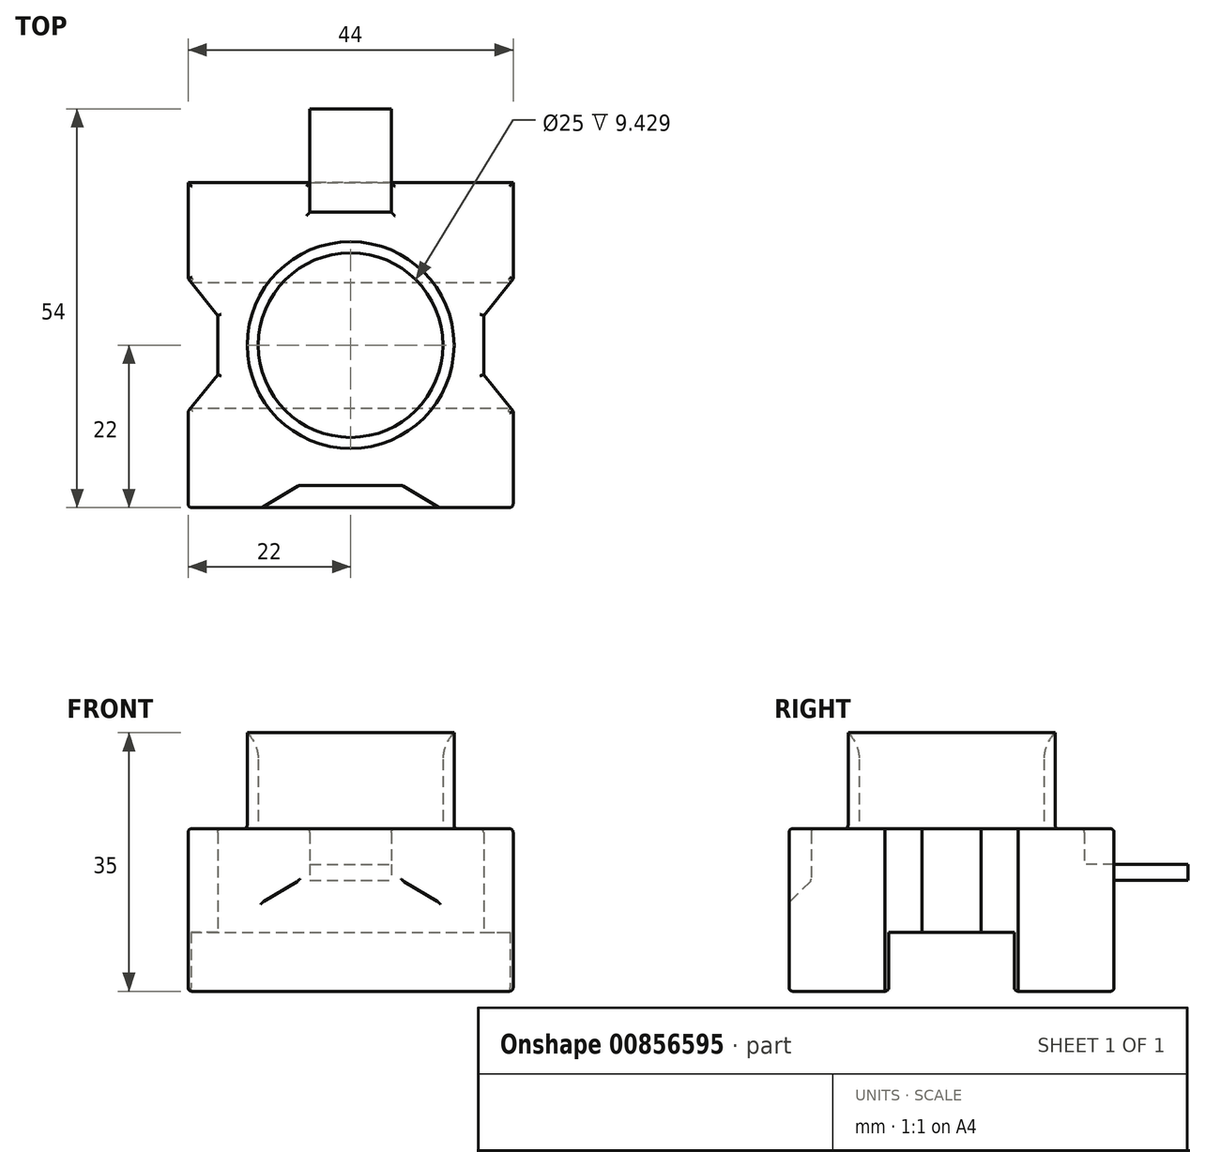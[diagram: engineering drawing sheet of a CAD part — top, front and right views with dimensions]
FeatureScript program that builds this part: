
annotation { "Feature Type Name" : "Feature", "Feature Type Description" : "" }
export const myFeature = defineFeature(function(context is Context, id is Id, definition is map)
    precondition{}
    {
        {
            var Q0;
            Q0=qCreatedBy(makeId("Top.planeOp"),FACE);
            var sketch = newSketch(context, id + "F0", { "sketchPlane" : qUnion([Q0])});
            skLineSegment(sketch, "E0.bottom", {"start": v(22, 22) * mm, "end": v(5.5, 22) * mm});
            skLineSegment(sketch, "E0.top", {"start": v(22, -22) * mm, "end": v(-22, -22) * mm});
            skLineSegment(sketch, "E0.left", {"start": v(22, 22) * mm, "end": v(22, -22) * mm});
            skLineSegment(sketch, "E0.right", {"start": v(-22, 22) * mm, "end": v(-22, 9) * mm});
            skPoint(sketch, "E0.middle", {"position": v(0, 0) * mm});
            skLineSegment(sketch, "E1.trimOffspring", {"start": v(-5.5, 22) * mm, "end": v(-22, 22) * mm});
            skLineSegment(sketch, "E2.MirrorCS", {"start": v(7, -19) * mm, "end": v(-7, -19) * mm});
            skLineSegment(sketch, "E3.MirrorCS", {"start": v(-12, -22) * mm, "end": v(-7, -19) * mm});
            skLineSegment(sketch, "E4.left", {"start": v(-18, 4) * mm, "end": v(-18, -4) * mm});
            skLineSegment(sketch, "E5", {"start": v(-22, 9) * mm, "end": v(-18, 4) * mm});
            skLineSegment(sketch, "E6.MirrorCS", {"start": v(-22, -9) * mm, "end": v(-18, -4) * mm});
            skLineSegment(sketch, "E7.trimOffspring", {"start": v(-22, -9) * mm, "end": v(-22, -22) * mm});
            skLineSegment(sketch, "E8.MirrorCS", {"start": v(22, 9) * mm, "end": v(18, 4) * mm});
            skLineSegment(sketch, "E9.MirrorCS", {"start": v(18, 4) * mm, "end": v(18, -4) * mm});
            skLineSegment(sketch, "E10.MirrorCS", {"start": v(22, -9) * mm, "end": v(18, -4) * mm});
            skLineSegment(sketch, "E11", {"start": v(-22, -9) * mm, "end": v(-22, 9) * mm});
            skLineSegment(sketch, "E12.bottom", {"start": v(5.5, 18) * mm, "end": v(-5.5, 18) * mm});
            skLineSegment(sketch, "E12.left", {"start": v(5.5, 18) * mm, "end": v(5.5, 22) * mm});
            skLineSegment(sketch, "E12.right", {"start": v(-5.5, 18) * mm, "end": v(-5.5, 22) * mm});
            skPoint(sketch, "E12.middle", {"position": v(0, 22) * mm});
            skPoint(sketch, "E13.orphan", {"position": v(-12, 22) * mm});
            skPoint(sketch, "E14.orphan", {"position": v(-5.5, 26) * mm});
            skPoint(sketch, "E15.orphan", {"position": v(5.5, 26) * mm});
            skLineSegment(sketch, "E16", {"start": v(-5.5, 22) * mm, "end": v(5.5, 22) * mm});
            skLineSegment(sketch, "E17.MirrorCS", {"start": v(12, -22) * mm, "end": v(7, -19) * mm});
            skSolve(sketch);
        }
        {
            var Q0;
            Q0=makeQuery(id+"F0.imprint","IMPRINT",FACE,{"disambiguationData":[TD([[makeQuery(id+"F0.imprint","IMPRINT",EDGE,{"derivedFrom":sQuery(id+"F0.wireOp",EDGE,"E0.bottom")}),1.0]])]});
            extrude(context, id + "F1", {"entities" : qUnion([Q0]), "depth" : 22 * mm, "offsetDistance" : 25 * mm});
        }
        {
            var Q0;
            Q0=makeQuery(id+"F0.imprint","IMPRINT",FACE,{"disambiguationData":[TD([[makeQuery(id+"F0.imprint","IMPRINT",EDGE,{"derivedFrom":sQuery(id+"F0.wireOp",EDGE,"E2.MirrorCS")}),1.0]])]});
            extrude(context, id + "F2", {"entities" : qUnion([Q0]), "operationType" : NewBodyOperationType.ADD, "depth" : 17 * mm, "offsetDistance" : 25 * mm});
        }
        {
            var Q0;
            Q0=makeQuery(id+"F2.opExtrude","CAP_EDGE",EDGE,{"disambiguationData":[OSD([sQuery(id+"F0.wireOp",EDGE,"E0.top")])],"isStart":false});
            chamfer(context, id + "F3", {"entities" : qUnion([Q0]), "width" : 5 * mm, "tangentPropagation" : true});
        }
        {
            var Q0;
            {var subQ0=sQuery(id+"F0.wireOp",EDGE,"E0.left");Q0=makeQuery(id+"F1.opExtrude","SWEPT_FACE",FACE,{"disambiguationData":[OSD([subQ0]),TDD([makeQuery(id+"F0.imprint","IMPRINT",EDGE,{"disambiguationData":[TD([[makeQuery(id+"F0.imprint","INTERSECT",VERTEX,{"derivedFrom":[sQuery(id+"F0.wireOp",EDGE,"E0.top"),subQ0]}),1.0]])],"derivedFrom":subQ0})])]});}
            var sketch = newSketch(context, id + "F4", { "sketchPlane" : qUnion([Q0])});
            skLineSegment(sketch, "E18", {"start": v(0, 0) * mm, "end": v(0, 4) * mm});
            skLineSegment(sketch, "E19.bottom", {"start": v(-8.5, 8) * mm, "end": v(8.5, 8) * mm});
            skLineSegment(sketch, "E19.top", {"start": v(-8.5, 0) * mm, "end": v(8.5, 0) * mm});
            skLineSegment(sketch, "E19.left", {"start": v(-8.5, 8) * mm, "end": v(-8.5, 0) * mm});
            skLineSegment(sketch, "E19.right", {"start": v(8.5, 8) * mm, "end": v(8.5, 0) * mm});
            skPoint(sketch, "E19.middle", {"position": v(0, 4) * mm});
            skSolve(sketch);
        }
        {
            var Q0;
            Q0=makeQuery(id+"F4.imprint","IMPRINT",FACE,{"disambiguationData":[TD([[makeQuery(id+"F4.imprint","IMPRINT",EDGE,{"derivedFrom":sQuery(id+"F4.wireOp",EDGE,"E19.bottom")}),-1.0]])]});
            var Q1;
            Q1=makeQuery(id+"F1.opExtrude","SWEPT_FACE",FACE,{"disambiguationData":[OSD([sQuery(id+"F0.wireOp",EDGE,"E0.right")])]});
            extrude(context, id + "F5", {"entities" : qUnion([Q0]), "operationType" : NewBodyOperationType.REMOVE, "endBound" : BoundingType.UP_TO_SURFACE, "oppositeDirection" : true, "depth" : 25 * mm, "endBoundEntityFace" : qUnion([Q1]), "offsetDistance" : 25 * mm});
        }
        {
            var Q0;
            Q0=makeQuery(id+"F0.imprint","IMPRINT",FACE,{"disambiguationData":[TD([[makeQuery(id+"F0.imprint","IMPRINT",EDGE,{"derivedFrom":sQuery(id+"F0.wireOp",EDGE,"E12.bottom")}),-1.0]])]});
            extrude(context, id + "F6", {"entities" : qUnion([Q0]), "operationType" : NewBodyOperationType.ADD, "depth" : 15 * mm, "offsetDistance" : 25 * mm});
        }
        {
            var Q0;
            Q0=makeQuery(id+"F1.opExtrude","SWEPT_FACE",FACE,{"disambiguationData":[OSD([sQuery(id+"F0.wireOp",EDGE,"E12.bottom")])]});
            var sketch = newSketch(context, id + "F7", { "sketchPlane" : qUnion([Q0])});
            skLineSegment(sketch, "E20.bottom", {"start": v(5.5, 15) * mm, "end": v(-5.5, 15) * mm});
            skLineSegment(sketch, "E20.top", {"start": v(5.5, 17.21) * mm, "end": v(-5.5, 17.21) * mm});
            skLineSegment(sketch, "E20.left", {"start": v(5.5, 15) * mm, "end": v(5.5, 17.21) * mm});
            skLineSegment(sketch, "E20.right", {"start": v(-5.5, 15) * mm, "end": v(-5.5, 17.21) * mm});
            skSolve(sketch);
        }
        {
            var Q0;
            Q0=makeQuery(id+"F7.imprint","IMPRINT",FACE,{"disambiguationData":[TD([[makeQuery(id+"F7.imprint","IMPRINT",EDGE,{"derivedFrom":sQuery(id+"F7.wireOp",EDGE,"E20.bottom")}),1.0]])]});
            extrude(context, id + "F8", {"entities" : qUnion([Q0]), "operationType" : NewBodyOperationType.ADD, "depth" : 14 * mm, "offsetDistance" : 25 * mm});
        }
        {
            var Q0;
            Q0=makeQuery(id+"F1.opExtrude","CAP_FACE",FACE,{"disambiguationData":[OSD([sQuery(id+"F0.wireOp",EDGE,"E0.bottom"),sQuery(id+"F0.wireOp",EDGE,"E0.top"),sQuery(id+"F0.wireOp",EDGE,"E0.left"),sQuery(id+"F0.wireOp",EDGE,"E0.right"),sQuery(id+"F0.wireOp",EDGE,"E1.trimOffspring"),sQuery(id+"F0.wireOp",EDGE,"E2.MirrorCS"),sQuery(id+"F0.wireOp",EDGE,"E3.MirrorCS"),sQuery(id+"F0.wireOp",EDGE,"E4.left"),sQuery(id+"F0.wireOp",EDGE,"E5"),sQuery(id+"F0.wireOp",EDGE,"E6.MirrorCS"),sQuery(id+"F0.wireOp",EDGE,"E7.trimOffspring"),sQuery(id+"F0.wireOp",EDGE,"E8.MirrorCS"),sQuery(id+"F0.wireOp",EDGE,"E9.MirrorCS"),sQuery(id+"F0.wireOp",EDGE,"E10.MirrorCS"),sQuery(id+"F0.wireOp",EDGE,"E12.bottom"),sQuery(id+"F0.wireOp",EDGE,"E12.left"),sQuery(id+"F0.wireOp",EDGE,"E12.right"),sQuery(id+"F0.wireOp",EDGE,"E17.MirrorCS")])],"isStart":false});
            var sketch = newSketch(context, id + "F9", { "sketchPlane" : qUnion([Q0])});
            skCircle(sketch, "E21", {"center": v(0, 0) * mm, "radius": 14 * mm});
            skCircle(sketch, "E22", {"center": v(0, 0) * mm, "radius": 12.5 * mm});
            skSolve(sketch);
        }
        {
            var Q0;
            Q0=makeQuery(id+"F9.imprint","IMPRINT",FACE,{"disambiguationData":[TD([[makeQuery(id+"F9.imprint","IMPRINT",EDGE,{"derivedFrom":sQuery(id+"F9.wireOp",EDGE,"E21")}),1.0]])]});
            extrude(context, id + "F10", {"entities" : qUnion([Q0]), "operationType" : NewBodyOperationType.ADD, "depth" : 13 * mm, "offsetDistance" : 25 * mm});
        }
        {
            var Q0;
            Q0=makeQuery(id+"F10.opExtrude","CAP_EDGE",EDGE,{"disambiguationData":[OSD([sQuery(id+"F9.wireOp",EDGE,"E22")])],"isStart":false});
            fillet(context, id + "F11", {"entities" : qUnion([Q0]), "radius" : 5 * mm, "tangentPropagation" : true, "allowEdgeOverflow" : false});
        }
        {
            var Q0;
            {var subQ0=sQuery(id+"F0.wireOp",EDGE,"E17.MirrorCS");var subQ1=sQuery(id+"F0.wireOp",EDGE,"E12.right");var subQ2=sQuery(id+"F0.wireOp",EDGE,"E12.left");var subQ3=sQuery(id+"F0.wireOp",EDGE,"E12.bottom");var subQ4=sQuery(id+"F0.wireOp",EDGE,"E10.MirrorCS");var subQ5=sQuery(id+"F0.wireOp",EDGE,"E9.MirrorCS");var subQ6=sQuery(id+"F0.wireOp",EDGE,"E8.MirrorCS");var subQ7=sQuery(id+"F0.wireOp",EDGE,"E7.trimOffspring");var subQ8=sQuery(id+"F0.wireOp",EDGE,"E6.MirrorCS");var subQ9=sQuery(id+"F0.wireOp",EDGE,"E5");var subQ10=sQuery(id+"F0.wireOp",EDGE,"E0.top");var subQ11=sQuery(id+"F0.wireOp",EDGE,"E3.MirrorCS");var subQ12=sQuery(id+"F0.wireOp",EDGE,"E0.left");var subQ14=sQuery(id+"F0.wireOp",EDGE,"E0.bottom");var subQ15=sQuery(id+"F0.wireOp",EDGE,"E4.left");var subQ16=sQuery(id+"F0.wireOp",EDGE,"E0.right");var subQ17=sQuery(id+"F0.wireOp",EDGE,"E1.trimOffspring");var subQ18=sQuery(id+"F0.wireOp",EDGE,"E2.MirrorCS");Q0=makeQuery(id+"F10.boolean.opBoolean","SPLIT",FACE,{"disambiguationData":[TD([makeQuery(id+"F1.opExtrude","SWEPT_FACE",FACE,{"disambiguationData":[OSD([subQ14])]})])],"derivedFrom":makeQuery(id+"F1.opExtrude","CAP_FACE",FACE,{"disambiguationData":[OSD([subQ14,subQ10,subQ12,subQ16,subQ17,subQ18,subQ11,subQ15,subQ9,subQ8,subQ7,subQ6,subQ5,subQ4,subQ3,subQ2,subQ1,subQ0])],"isStart":false})});}
            var Q1;
            {var subQ0=sQuery(id+"F0.wireOp",EDGE,"E12.right");var subQ1=sQuery(id+"F0.wireOp",EDGE,"E12.left");var subQ2=sQuery(id+"F0.wireOp",EDGE,"E12.bottom");var subQ3=sQuery(id+"F0.wireOp",EDGE,"E1.trimOffspring");var subQ4=sQuery(id+"F0.wireOp",EDGE,"E0.right");var subQ5=sQuery(id+"F0.wireOp",EDGE,"E0.left");var subQ6=sQuery(id+"F0.wireOp",EDGE,"E0.bottom");var subQ7=sQuery(id+"F0.wireOp",EDGE,"E8.MirrorCS");var subQ8=sQuery(id+"F0.wireOp",EDGE,"E5");var subQ9=sQuery(id+"F0.wireOp",EDGE,"E17.MirrorCS");var subQ10=sQuery(id+"F0.wireOp",EDGE,"E3.MirrorCS");var subQ11=sQuery(id+"F0.wireOp",EDGE,"E2.MirrorCS");var subQ12=sQuery(id+"F0.wireOp",EDGE,"E0.top");Q1=makeQuery(id+"F6.boolean.opBoolean","MERGE",FACE,{"derivedFrom":[makeQuery(id+"F5.boolean.opBoolean","SPLIT",FACE,{"disambiguationData":[TD([makeQuery(id+"F1.opExtrude","SWEPT_FACE",FACE,{"disambiguationData":[OSD([subQ6])]})])],"derivedFrom":makeQuery(id+"F2.boolean.opBoolean","MERGE",FACE,{"derivedFrom":[makeQuery(id+"F1.opExtrude","CAP_FACE",FACE,{"disambiguationData":[OSD([subQ6,subQ12,subQ5,subQ4,subQ3,subQ11,subQ10,sQuery(id+"F0.wireOp",EDGE,"E4.left"),subQ8,sQuery(id+"F0.wireOp",EDGE,"E6.MirrorCS"),sQuery(id+"F0.wireOp",EDGE,"E7.trimOffspring"),subQ7,sQuery(id+"F0.wireOp",EDGE,"E9.MirrorCS"),sQuery(id+"F0.wireOp",EDGE,"E10.MirrorCS"),subQ2,subQ1,subQ0,subQ9])],"isStart":true}),makeQuery(id+"F2.opExtrude","CAP_FACE",FACE,{"disambiguationData":[OSD([subQ12,subQ11,subQ10,subQ9])],"isStart":true})]})}),makeQuery(id+"F6.opExtrude","CAP_FACE",FACE,{"disambiguationData":[OSD([subQ2,subQ1,subQ0,sQuery(id+"F0.wireOp",EDGE,"E16")])],"isStart":true})]});}
            var Q2;
            {var subQ0=sQuery(id+"F0.wireOp",EDGE,"E0.left");var subQ1=sQuery(id+"F0.wireOp",EDGE,"E0.top");var subQ3=sQuery(id+"F0.wireOp",EDGE,"E10.MirrorCS");var subQ4=sQuery(id+"F0.wireOp",EDGE,"E7.trimOffspring");var subQ5=sQuery(id+"F0.wireOp",EDGE,"E3.MirrorCS");var subQ6=sQuery(id+"F0.wireOp",EDGE,"E6.MirrorCS");var subQ7=sQuery(id+"F0.wireOp",EDGE,"E17.MirrorCS");var subQ8=sQuery(id+"F0.wireOp",EDGE,"E2.MirrorCS");Q2=makeQuery(id+"F5.boolean.opBoolean","SPLIT",FACE,{"disambiguationData":[TD([makeQuery(id+"F1.opExtrude","SWEPT_FACE",FACE,{"disambiguationData":[OSD([subQ6])]})])],"derivedFrom":makeQuery(id+"F2.boolean.opBoolean","MERGE",FACE,{"derivedFrom":[makeQuery(id+"F1.opExtrude","CAP_FACE",FACE,{"disambiguationData":[OSD([sQuery(id+"F0.wireOp",EDGE,"E0.bottom"),subQ1,subQ0,sQuery(id+"F0.wireOp",EDGE,"E0.right"),sQuery(id+"F0.wireOp",EDGE,"E1.trimOffspring"),subQ8,subQ5,sQuery(id+"F0.wireOp",EDGE,"E4.left"),sQuery(id+"F0.wireOp",EDGE,"E5"),subQ6,subQ4,sQuery(id+"F0.wireOp",EDGE,"E8.MirrorCS"),sQuery(id+"F0.wireOp",EDGE,"E9.MirrorCS"),subQ3,sQuery(id+"F0.wireOp",EDGE,"E12.bottom"),sQuery(id+"F0.wireOp",EDGE,"E12.left"),sQuery(id+"F0.wireOp",EDGE,"E12.right"),subQ7])],"isStart":true}),makeQuery(id+"F2.opExtrude","CAP_FACE",FACE,{"disambiguationData":[OSD([subQ1,subQ8,subQ5,subQ7])],"isStart":true})]})});}
            var Q3;
            Q3=makeQuery(id+"F1.opExtrude","SWEPT_FACE",FACE,{"disambiguationData":[OSD([sQuery(id+"F0.wireOp",EDGE,"E2.MirrorCS")])]});
            var Q4;
            {var subQ0=sQuery(id+"F0.wireOp",EDGE,"E0.top");Q4=makeQuery(id+"F2.boolean.opBoolean","MERGE",FACE,{"derivedFrom":[makeQuery(id+"F1.opExtrude","SWEPT_FACE",FACE,{"disambiguationData":[OSD([subQ0]),TDD([makeQuery(id+"F0.imprint","IMPRINT",EDGE,{"disambiguationData":[TD([[makeQuery(id+"F0.imprint","INTERSECT",VERTEX,{"derivedFrom":[subQ0,sQuery(id+"F0.wireOp",EDGE,"E0.left")]}),-1.0]])],"derivedFrom":subQ0})])]}),makeQuery(id+"F1.opExtrude","SWEPT_FACE",FACE,{"disambiguationData":[OSD([subQ0]),TDD([makeQuery(id+"F0.imprint","IMPRINT",EDGE,{"disambiguationData":[TD([[makeQuery(id+"F0.imprint","INTERSECT",VERTEX,{"derivedFrom":[subQ0,sQuery(id+"F0.wireOp",EDGE,"E7.trimOffspring")]}),1.0]])],"derivedFrom":subQ0})])]}),makeQuery(id+"F2.opExtrude","SWEPT_FACE",FACE,{"disambiguationData":[OSD([subQ0])]})]});}
            var Q5;
            Q5=makeQuery(id+"F1.opExtrude","SWEPT_FACE",FACE,{"disambiguationData":[OSD([sQuery(id+"F0.wireOp",EDGE,"E7.trimOffspring")])]});
            fillet(context, id + "F12", {"entities" : qUnion([Q0, Q1, Q2, Q3, Q4, Q5]), "radius" : .5 * mm, "tangentPropagation" : true, "allowEdgeOverflow" : false});
        }
    });
